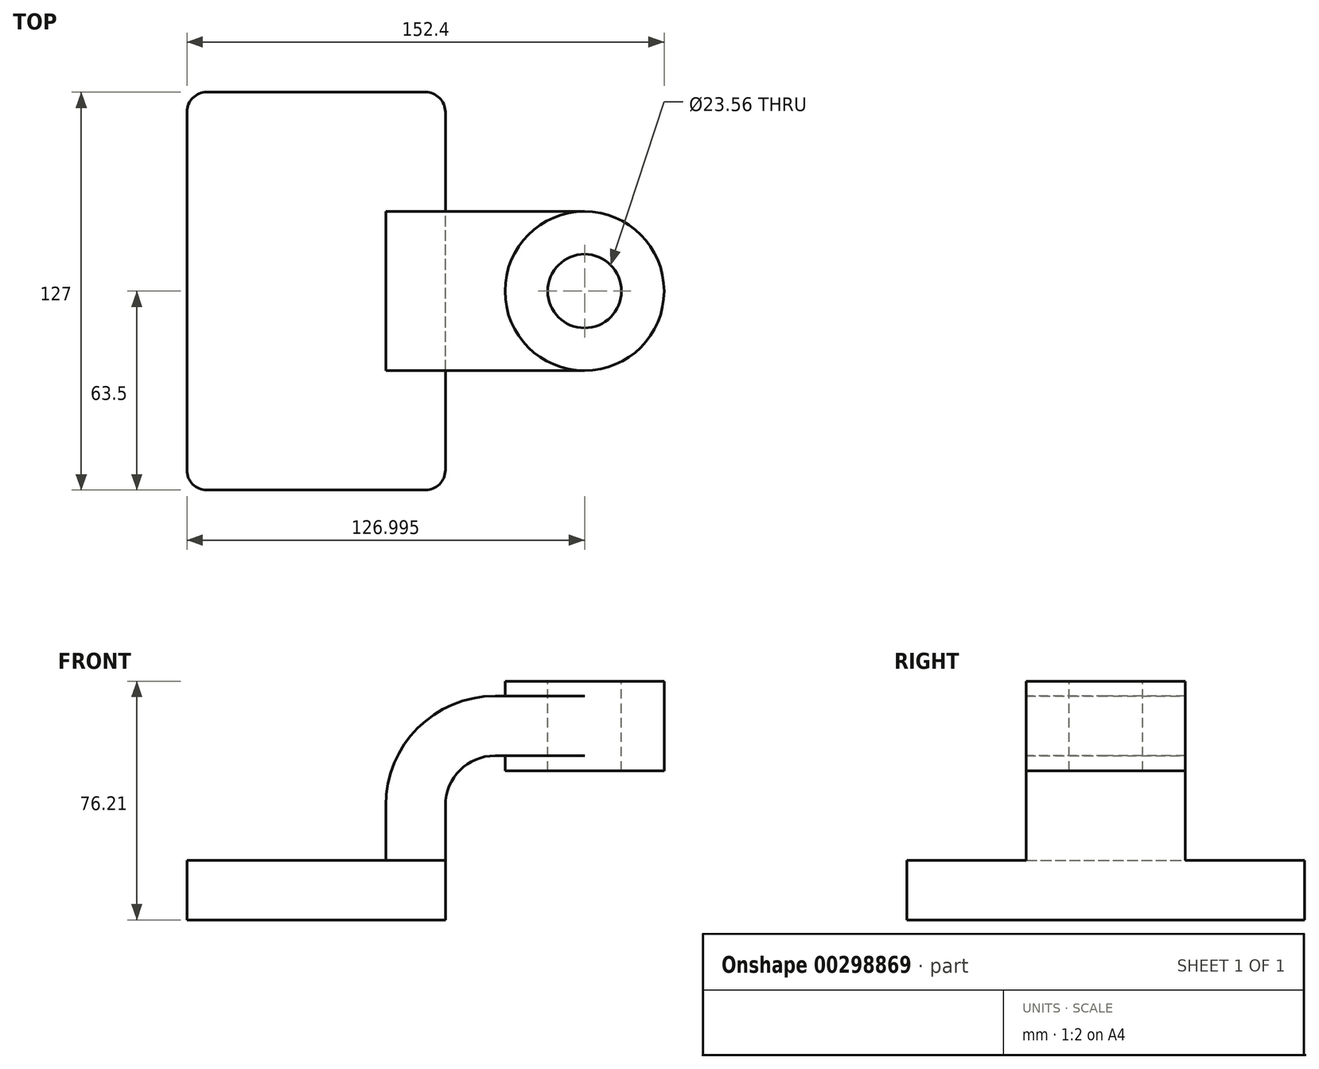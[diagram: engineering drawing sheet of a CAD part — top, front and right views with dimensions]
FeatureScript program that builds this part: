
annotation { "Feature Type Name" : "Feature", "Feature Type Description" : "" }
export const myFeature = defineFeature(function(context is Context, id is Id, definition is map)
    precondition{}
    {
        {
            var Q0;
            Q0=qCreatedBy(makeId("Front.planeOp"),FACE);
            var sketch = newSketch(context, id + "F0", { "sketchPlane" : qUnion([Q0])});
            skLineSegment(sketch, "E0.bottom", {"start": v(-41.27, -9.53) * mm, "end": v(41.28, -9.53) * mm});
            skLineSegment(sketch, "E0.top", {"start": v(-41.28, 9.53) * mm, "end": v(41.28, 9.53) * mm});
            skLineSegment(sketch, "E0.left", {"start": v(-41.28, -9.53) * mm, "end": v(-41.28, 9.53) * mm});
            skLineSegment(sketch, "E0.right", {"start": v(41.28, -9.53) * mm, "end": v(41.28, 9.53) * mm});
            skPoint(sketch, "E0.middle", {"position": v(0, 0) * mm});
            skLineSegment(sketch, "E1.bottom", {"start": v(60.33, 38.1) * mm, "end": v(111.12, 38.1) * mm});
            skLineSegment(sketch, "E1.top", {"start": v(60.33, 66.68) * mm, "end": v(111.12, 66.68) * mm});
            skLineSegment(sketch, "E1.left", {"start": v(60.33, 38.1) * mm, "end": v(60.33, 66.68) * mm});
            skLineSegment(sketch, "E1.right", {"start": v(111.12, 38.1) * mm, "end": v(111.12, 66.68) * mm});
            skPoint(sketch, "E1.middle", {"position": v(85.72, 52.39) * mm});
            skLineSegment(sketch, "E2", {"start": v(41.28, 9.53) * mm, "end": v(41.28, 27) * mm});
            skArc(sketch, "E3", {"start": v(41.27, 27) * mm, "mid": v(45.92, 38.23) * mm, "end": v(57.15, 42.88) * mm});
            skLineSegment(sketch, "E4", {"start": v(57.15, 42.88) * mm, "end": v(85.72, 42.88) * mm});
            skLineSegment(sketch, "E5.0", {"start": v(57.15, 61.93) * mm, "end": v(85.72, 61.93) * mm});
            skArc(sketch, "E5.1", {"start": v(22.22, 27) * mm, "mid": v(32.45, 51.7) * mm, "end": v(57.15, 61.93) * mm});
            skLineSegment(sketch, "E5.2", {"start": v(22.22, 9.53) * mm, "end": v(22.22, 27) * mm});
            skLineSegment(sketch, "E6", {"start": v(85.72, 38.1) * mm, "end": v(85.72, 66.68) * mm});
            skFitSpline(sketch, "E7", {"points": [v(-41.28, 9.53) * mm, v(57.15, 61.93) * mm], "startDerivative": vector(0, 58.46) * mm, "endDerivative": vector(112.53, 0) * mm});
            skSolve(sketch);
        }
        {
            var Q0;
            Q0=makeQuery(id+"F0.imprint","IMPRINT",FACE,{"disambiguationData":[TD([[makeQuery(id+"F0.imprint","IMPRINT",EDGE,{"derivedFrom":sQuery(id+"F0.wireOp",EDGE,"E0.bottom")}),1.0]])]});
            extrude(context, id + "F1", {"entities" : qUnion([Q0]), "endBound" : BoundingType.SYMMETRIC, "depth" : 127 * mm});
        }
        {
            var Q0;
            {var subQ1=sQuery(id+"F0.wireOp",EDGE,"E2");Q0=makeQuery(id+"F0.imprint","IMPRINT",FACE,{"disambiguationData":[TD([[makeQuery(id+"F0.imprint","IMPRINT",EDGE,{"derivedFrom":subQ1}),1.0]])]});}
            var Q1;
            {var subQ0=sQuery(id+"F0.wireOp",EDGE,"E4");var subQ1=sQuery(id+"F0.wireOp",EDGE,"E1.left");var subQ2=makeQuery(id+"F0.imprint","INTERSECT",VERTEX,{"derivedFrom":[subQ1,subQ0]});Q1=makeQuery(id+"F0.imprint","IMPRINT",FACE,{"disambiguationData":[TD([[makeQuery(id+"F0.imprint","IMPRINT",EDGE,{"disambiguationData":[TD([[subQ2,-1.0]])],"derivedFrom":subQ1}),-1.0]])]});}
            extrude(context, id + "F2", {"entities" : qUnion([Q0, Q1]), "operationType" : NewBodyOperationType.ADD, "endBound" : BoundingType.SYMMETRIC, "depth" : 50.8 * mm});
        }
        {
            var Q0;
            Q0=makeQuery(id+"F0.imprint","IMPRINT",FACE,{"disambiguationData":[TD([[makeQuery(id+"F0.imprint","IMPRINT",EDGE,{"derivedFrom":sQuery(id+"F0.wireOp",EDGE,"E5.1")}),1.0]])]});
            extrude(context, id + "F3", {"entities" : qUnion([Q0]), "operationType" : NewBodyOperationType.ADD, "endBound" : BoundingType.SYMMETRIC, "depth" : 15.88 * mm});
        }
        {
            var Q0;
            {var subQ0=sQuery(id+"F0.wireOp",EDGE,"E1.right");Q0=makeQuery(id+"F0.imprint","IMPRINT",FACE,{"disambiguationData":[TD([[makeQuery(id+"F0.imprint","IMPRINT",EDGE,{"derivedFrom":subQ0}),1.0]])]});}
            var Q1;
            Q1=sQuery(id+"F0.wireOp",EDGE,"E6");
            revolve(context, id + "F4", {"operationType" : NewBodyOperationType.ADD, "entities" : qUnion([Q0]), "axis" : qUnion([Q1]), "revolveType" : RevolveType.FULL});
        }
        {
            var Q0;
            Q0=makeQuery(id+"F1.opExtrude","CAP_EDGE",EDGE,{"disambiguationData":[OSD([sQuery(id+"F0.wireOp",EDGE,"E0.right")])],"isStart":false});
            var Q1;
            Q1=makeQuery(id+"F1.opExtrude","CAP_EDGE",EDGE,{"disambiguationData":[OSD([sQuery(id+"F0.wireOp",EDGE,"E0.left")])],"isStart":false});
            var Q2;
            Q2=makeQuery(id+"F1.opExtrude","CAP_EDGE",EDGE,{"disambiguationData":[OSD([sQuery(id+"F0.wireOp",EDGE,"E0.left")])],"isStart":true});
            var Q3;
            Q3=makeQuery(id+"F1.opExtrude","CAP_EDGE",EDGE,{"disambiguationData":[OSD([sQuery(id+"F0.wireOp",EDGE,"E0.right")])],"isStart":true});
            fillet(context, id + "F5", {"entities" : qUnion([Q0, Q1, Q2, Q3]), "radius" : 6.35 * mm, "tangentPropagation" : true, "allowEdgeOverflow" : false});
        }
        {
            var Q0;
            Q0=makeQuery(id+"F4.opRevolve","SWEPT_FACE",FACE,{"disambiguationData":[OSD([sQuery(id+"F0.wireOp",EDGE,"E1.top")])]});
            var sketch = newSketch(context, id + "F6", { "sketchPlane" : qUnion([Q0])});
            skCircle(sketch, "E8", {"center": v(85.72, 0) * mm, "radius": 11.78 * mm});
            skSolve(sketch);
        }
        {
            var Q0;
            Q0 = qSketchRegion(id + "F6", true);
            extrude(context, id + "F7", {"entities" : qUnion([Q0]), "operationType" : NewBodyOperationType.REMOVE, "endBound" : BoundingType.UP_TO_NEXT, "oppositeDirection" : true, "depth" : 17.27 * mm});
        }
    });
